# Revit family: Accessory-Tissue_Holder-KOHLER-Castia-K-35929_1
name_source: partatom
category: Specialty Equipment
units: mm (PartAtom-declared; Revit-internal decimal feet)

## family parameters
Cut with Voids When Loaded = No
Host = Face
OmniClass Number = 23.31.25.00
OmniClass Title = Toilet and Bath Specialties
Part Type = Normal
Room Calculation Point = No
Round Connector Dimension = Use Diameter
Shared = No

## types (5) — shared parameters
ADA Compliant = No
Assembly Code = C1030200
Date Modified = 03/30/2023
Default Elevation = 42"
Description = Toilet Tissue Holder
Height = 2 1/2"
Length = 6 7/16"
Manufacturer = Kohler Co.
Master Format 2014 = 10 28 00
Master Format 2014 Name = Toilet, Bath, and Laundry Accessories
Material = Premium Metal Construction
Product Documentation Link = https://www.us.kohler.com
Product Name = Castia
Product Page URL = http://www.us.kohler.com
URL = https://www.us.kohler.com
WaterSense Certified = No
Width = 4 1/16"

## per-type parameters (varying)
| type | Finish | Model | Type |
| 2MB-Vibrant Brushed Moderne Bras | Kohler-Metal-2MB-Vibrant_Brushed_Moderne_Brass | K-35929-2MB | 1 |
| BL-Matte Black | Kohler-Metal-BL-Matte_Black | K-35929-BL | 2 |
| BN-Vibrant Brushed Nickel | Kohler-Metal-BN-Vibrant_Brushed_Nickel | K-35929-BN | 3 |
| CP-Polished Chrome | Kohler-Metal-CP-Polished_Chrome | K-35929-CP | 4 |
| SN-Vibrant Polished Nickel | Kohler-Metal-SN-Vibrant_Polished_Nickel | K-35929-SN | 5 |

## geometry (parser evidence)
native form markers: Sweep x5
no freeform markers — native parametric forms only
